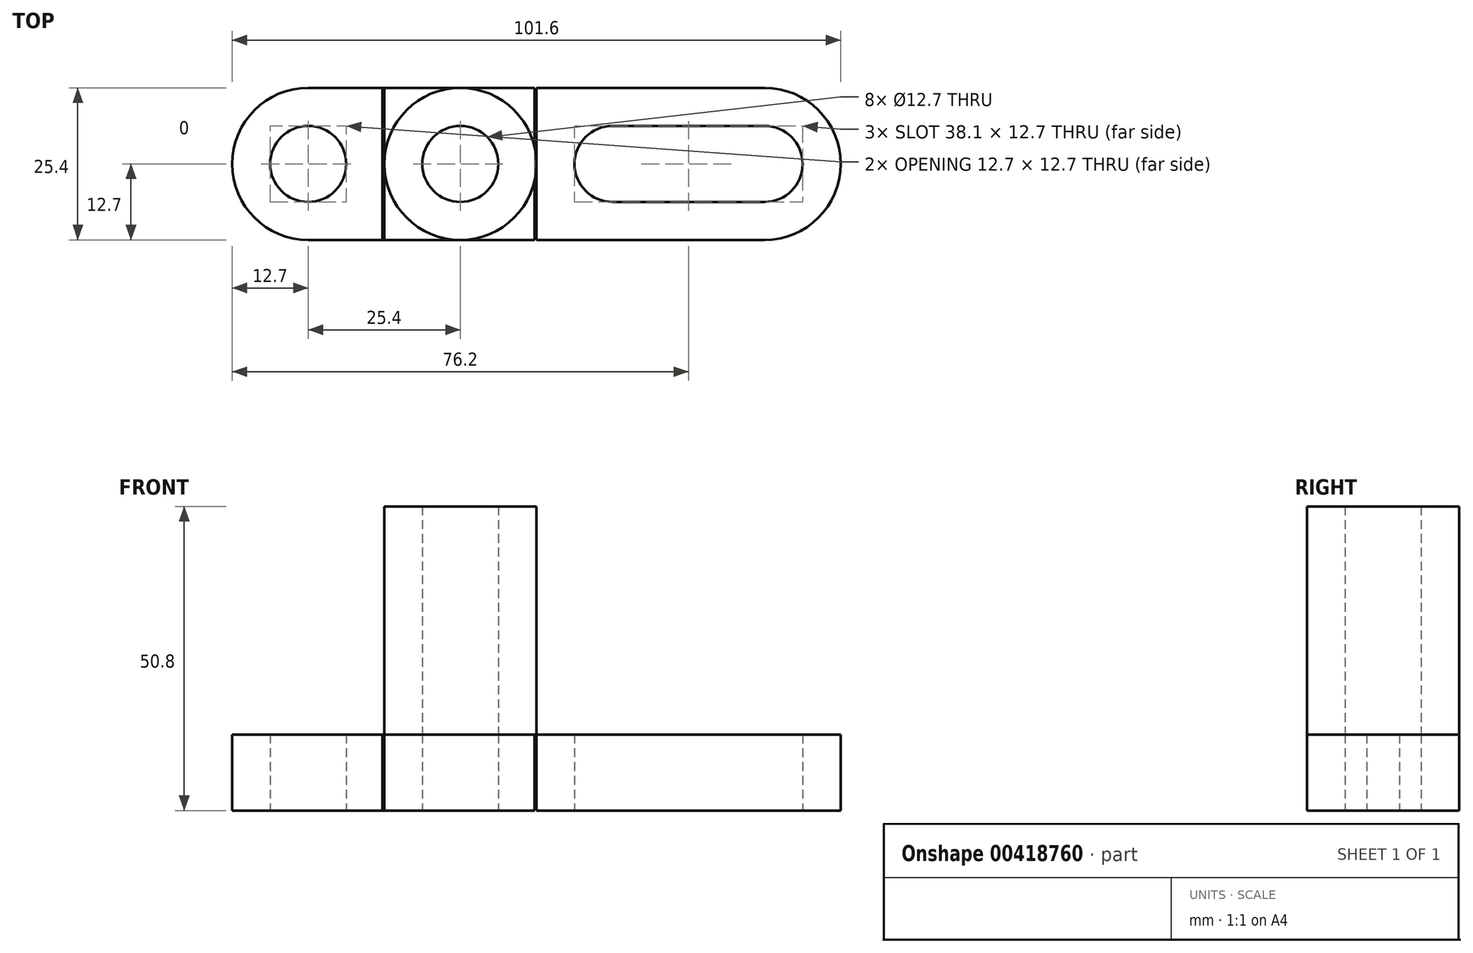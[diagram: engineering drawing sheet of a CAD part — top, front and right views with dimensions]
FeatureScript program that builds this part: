
annotation { "Feature Type Name" : "Feature", "Feature Type Description" : "" }
export const myFeature = defineFeature(function(context is Context, id is Id, definition is map)
    precondition{}
    {
        {
            var Q0;
            Q0=qCreatedBy(makeId("Front.planeOp"),FACE);
            var sketch = newSketch(context, id + "F0", { "sketchPlane" : qUnion([Q0])});
            skLineSegment(sketch, "E0", {"start": v(0, 0) * mm, "end": v(101.6, 0) * mm});
            skLineSegment(sketch, "E1", {"start": v(101.6, 0) * mm, "end": v(101.6, 12.7) * mm});
            skLineSegment(sketch, "E2", {"start": v(101.6, 12.7) * mm, "end": v(0, 12.7) * mm});
            skLineSegment(sketch, "E3", {"start": v(0, 12.7) * mm, "end": v(0, 0) * mm});
            skLineSegment(sketch, "E4", {"start": v(25.4, 0) * mm, "end": v(25.4, 50.8) * mm});
            skLineSegment(sketch, "E5", {"start": v(25.4, 50.8) * mm, "end": v(50.8, 50.8) * mm});
            skLineSegment(sketch, "E6", {"start": v(50.8, 50.8) * mm, "end": v(50.8, 0) * mm});
            skLineSegment(sketch, "E7", {"start": v(50.8, 0) * mm, "end": v(25.4, 0) * mm});
            skSolve(sketch);
        }
        {
            var Q0;
            {var subQ0=sQuery(id+"F0.wireOp",EDGE,"E3");Q0=makeQuery(id+"F0.imprint","IMPRINT",FACE,{"disambiguationData":[TD([[makeQuery(id+"F0.imprint","IMPRINT",EDGE,{"derivedFrom":subQ0}),1.0]])]});}
            var Q1;
            {var subQ5=sQuery(id+"F0.wireOp",EDGE,"E7");Q1=makeQuery(id+"F0.imprint","IMPRINT",FACE,{"disambiguationData":[TD([[makeQuery(id+"F0.imprint","IMPRINT",EDGE,{"derivedFrom":subQ5}),-1.0]])]});}
            var Q2;
            {var subQ5=sQuery(id+"F0.wireOp",EDGE,"E5");Q2=makeQuery(id+"F0.imprint","IMPRINT",FACE,{"disambiguationData":[TD([[makeQuery(id+"F0.imprint","IMPRINT",EDGE,{"derivedFrom":subQ5}),-1.0]])]});}
            var Q3;
            {var subQ0=sQuery(id+"F0.wireOp",EDGE,"E1");Q3=makeQuery(id+"F0.imprint","IMPRINT",FACE,{"disambiguationData":[TD([[makeQuery(id+"F0.imprint","IMPRINT",EDGE,{"derivedFrom":subQ0}),1.0]])]});}
            extrude(context, id + "F1", {"entities" : qUnion([Q0, Q1, Q2, Q3]), "depth" : 25.4 * mm});
        }
        {
            var Q0;
            Q0=qCreatedBy(makeId("Top.planeOp"),FACE);
            var sketch = newSketch(context, id + "F2", { "sketchPlane" : qUnion([Q0])});
            skCircle(sketch, "E8", {"center": v(12.7, -12.7) * mm, "radius": 6.35 * mm});
            skCircle(sketch, "E9", {"center": v(38.1, -12.7) * mm, "radius": 6.35 * mm});
            skCircle(sketch, "E10", {"center": v(63.5, -12.7) * mm, "radius": 6.35 * mm});
            skCircle(sketch, "E11", {"center": v(88.9, -12.7) * mm, "radius": 6.35 * mm});
            skLineSegment(sketch, "E12", {"start": v(63.5, -6.35) * mm, "end": v(88.9, -6.35) * mm});
            skLineSegment(sketch, "E13", {"start": v(88.9, -6.35) * mm, "end": v(88.9, -19.05) * mm});
            skLineSegment(sketch, "E14", {"start": v(88.9, -19.05) * mm, "end": v(63.5, -19.05) * mm});
            skLineSegment(sketch, "E15", {"start": v(63.5, -19.05) * mm, "end": v(63.5, -6.35) * mm});
            skPoint(sketch, "E16.endSnap0", {"position": v(101.6, -12.7) * mm});
            skArc(sketch, "E17", {"start": v(12.7, 0) * mm, "mid": v(0, -12.7) * mm, "end": v(12.7, -25.4) * mm});
            skLineSegment(sketch, "E18", {"start": v(12.7, -25.4) * mm, "end": v(0, -25.4) * mm});
            skLineSegment(sketch, "E19", {"start": v(0, -25.4) * mm, "end": v(0, 0) * mm});
            skLineSegment(sketch, "E20", {"start": v(0, 0) * mm, "end": v(12.7, 0) * mm});
            skArc(sketch, "E21", {"start": v(88.9, 0) * mm, "mid": v(101.6, -12.7) * mm, "end": v(88.9, -25.4) * mm});
            skLineSegment(sketch, "E22", {"start": v(88.9, -25.4) * mm, "end": v(101.6, -25.4) * mm});
            skLineSegment(sketch, "E23", {"start": v(101.6, -25.4) * mm, "end": v(101.6, 0) * mm});
            skLineSegment(sketch, "E24", {"start": v(101.6, 0) * mm, "end": v(88.9, 0) * mm});
            skCircle(sketch, "E25", {"center": v(38.1, -12.7) * mm, "radius": 12.7 * mm});
            skLineSegment(sketch, "E26", {"start": v(25.4, 0) * mm, "end": v(50.8, 0) * mm});
            skPoint(sketch, "E26.startSnap0", {"position": v(95.25, 0) * mm});
            skLineSegment(sketch, "E27", {"start": v(50.8, 0) * mm, "end": v(50.8, -25.4) * mm});
            skLineSegment(sketch, "E28", {"start": v(50.8, -25.4) * mm, "end": v(25.4, -25.4) * mm});
            skLineSegment(sketch, "E29", {"start": v(25.4, -25.4) * mm, "end": v(25.4, 0) * mm});
            skSolve(sketch);
        }
        {
            var Q0;
            {var subQ0=sQuery(id+"F2.wireOp",EDGE,"E13");Q0=makeQuery(id+"F2.imprint","IMPRINT",FACE,{"disambiguationData":[TD([[makeQuery(id+"F2.imprint","IMPRINT",EDGE,{"derivedFrom":subQ0}),1.0]])]});}
            var Q1;
            {var subQ0=sQuery(id+"F2.wireOp",EDGE,"E13");Q1=makeQuery(id+"F2.imprint","IMPRINT",FACE,{"disambiguationData":[TD([[makeQuery(id+"F2.imprint","IMPRINT",EDGE,{"derivedFrom":subQ0}),-1.0]])]});}
            var Q2;
            {var subQ1=sQuery(id+"F2.wireOp",EDGE,"E12");Q2=makeQuery(id+"F2.imprint","IMPRINT",FACE,{"disambiguationData":[TD([[makeQuery(id+"F2.imprint","IMPRINT",EDGE,{"derivedFrom":subQ1}),-1.0]])]});}
            var Q3;
            {var subQ0=sQuery(id+"F2.wireOp",EDGE,"E15");Q3=makeQuery(id+"F2.imprint","IMPRINT",FACE,{"disambiguationData":[TD([[makeQuery(id+"F2.imprint","IMPRINT",EDGE,{"derivedFrom":subQ0}),-1.0]])]});}
            var Q4;
            {var subQ0=sQuery(id+"F2.wireOp",EDGE,"E15");Q4=makeQuery(id+"F2.imprint","IMPRINT",FACE,{"disambiguationData":[TD([[makeQuery(id+"F2.imprint","IMPRINT",EDGE,{"derivedFrom":subQ0}),1.0]])]});}
            var Q5;
            Q5=makeQuery(id+"F2.imprint","IMPRINT",FACE,{"disambiguationData":[TD([[makeQuery(id+"F2.imprint","IMPRINT",EDGE,{"derivedFrom":sQuery(id+"F2.wireOp",EDGE,"E9")}),1.0]])]});
            var Q6;
            Q6=makeQuery(id+"F2.imprint","IMPRINT",FACE,{"disambiguationData":[TD([[makeQuery(id+"F2.imprint","IMPRINT",EDGE,{"derivedFrom":sQuery(id+"F2.wireOp",EDGE,"E8")}),1.0]])]});
            var Q7;
            {var subQ0=sQuery(id+"F2.wireOp",EDGE,"E18");Q7=makeQuery(id+"F2.imprint","IMPRINT",FACE,{"disambiguationData":[TD([[makeQuery(id+"F2.imprint","IMPRINT",EDGE,{"derivedFrom":subQ0}),-1.0]])]});}
            var Q8;
            {var subQ0=sQuery(id+"F2.wireOp",EDGE,"E20");Q8=makeQuery(id+"F2.imprint","IMPRINT",FACE,{"disambiguationData":[TD([[makeQuery(id+"F2.imprint","IMPRINT",EDGE,{"derivedFrom":subQ0}),-1.0]])]});}
            var Q9;
            {var subQ0=sQuery(id+"F2.wireOp",EDGE,"E22");Q9=makeQuery(id+"F2.imprint","IMPRINT",FACE,{"disambiguationData":[TD([[makeQuery(id+"F2.imprint","IMPRINT",EDGE,{"derivedFrom":subQ0}),1.0]])]});}
            var Q10;
            {var subQ0=sQuery(id+"F2.wireOp",EDGE,"E24");Q10=makeQuery(id+"F2.imprint","IMPRINT",FACE,{"disambiguationData":[TD([[makeQuery(id+"F2.imprint","IMPRINT",EDGE,{"derivedFrom":subQ0}),1.0]])]});}
            var Q11;
            {var subQ0=sQuery(id+"F2.wireOp",EDGE,"E27");var subQ1=sQuery(id+"F2.wireOp",EDGE,"E25");var subQ2=makeQuery(id+"F2.imprint","INTERSECT",VERTEX,{"derivedFrom":[subQ1,subQ0]});Q11=makeQuery(id+"F2.imprint","IMPRINT",FACE,{"disambiguationData":[TD([[makeQuery(id+"F2.imprint","IMPRINT",EDGE,{"disambiguationData":[TD([[subQ2,1.0]])],"derivedFrom":subQ1}),-1.0]])]});}
            var Q12;
            {var subQ0=sQuery(id+"F2.wireOp",EDGE,"E29");var subQ1=sQuery(id+"F2.wireOp",EDGE,"E25");var subQ2=makeQuery(id+"F2.imprint","INTERSECT",VERTEX,{"disambiguationData":[OD(1.0)],"derivedFrom":[subQ1,subQ0]});Q12=makeQuery(id+"F2.imprint","IMPRINT",FACE,{"disambiguationData":[TD([[makeQuery(id+"F2.imprint","IMPRINT",EDGE,{"disambiguationData":[TD([[subQ2,-1.0]])],"derivedFrom":subQ1}),-1.0]])]});}
            var Q13;
            {var subQ0=sQuery(id+"F2.wireOp",EDGE,"E26");var subQ1=sQuery(id+"F2.wireOp",EDGE,"E25");var subQ2=makeQuery(id+"F2.imprint","INTERSECT",VERTEX,{"derivedFrom":[subQ1,subQ0]});Q13=makeQuery(id+"F2.imprint","IMPRINT",FACE,{"disambiguationData":[TD([[makeQuery(id+"F2.imprint","IMPRINT",EDGE,{"disambiguationData":[TD([[subQ2,-1.0]])],"derivedFrom":subQ1}),-1.0]])]});}
            var Q14;
            {var subQ0=sQuery(id+"F2.wireOp",EDGE,"E26");var subQ1=sQuery(id+"F2.wireOp",EDGE,"E25");var subQ2=makeQuery(id+"F2.imprint","INTERSECT",VERTEX,{"derivedFrom":[subQ1,subQ0]});Q14=makeQuery(id+"F2.imprint","IMPRINT",FACE,{"disambiguationData":[TD([[makeQuery(id+"F2.imprint","IMPRINT",EDGE,{"disambiguationData":[TD([[subQ2,1.0]])],"derivedFrom":subQ1}),-1.0]])]});}
            extrude(context, id + "F3", {"entities" : qUnion([Q0, Q1, Q2, Q3, Q4, Q5, Q6, Q7, Q8, Q9, Q10, Q11, Q12, Q13, Q14]), "operationType" : NewBodyOperationType.REMOVE, "depth" : 50.8 * mm});
        }
        {
            var Q0;
            Q0=qCreatedBy(makeId("Top.planeOp"),FACE);
            var sketch = newSketch(context, id + "F4", { "sketchPlane" : qUnion([Q0])});
            skLineSegment(sketch, "E30", {"start": v(25.1, 0) * mm, "end": v(50.5, 0) * mm});
            skLineSegment(sketch, "E31", {"start": v(50.5, 0) * mm, "end": v(50.5, -25.4) * mm});
            skLineSegment(sketch, "E32", {"start": v(50.5, -25.4) * mm, "end": v(25.1, -25.4) * mm});
            skLineSegment(sketch, "E33", {"start": v(25.1, -25.4) * mm, "end": v(25.1, 0) * mm});
            skSolve(sketch);
        }
        {
            var Q0;
            Q0=makeQuery(id+"F4.imprint","IMPRINT",FACE,{"disambiguationData":[TD([[makeQuery(id+"F4.imprint","IMPRINT",EDGE,{"derivedFrom":sQuery(id+"F4.wireOp",EDGE,"E30")}),-1.0]])]});
            extrude(context, id + "F5", {"entities" : qUnion([Q0]), "depth" : 12.7 * mm});
        }
    });
